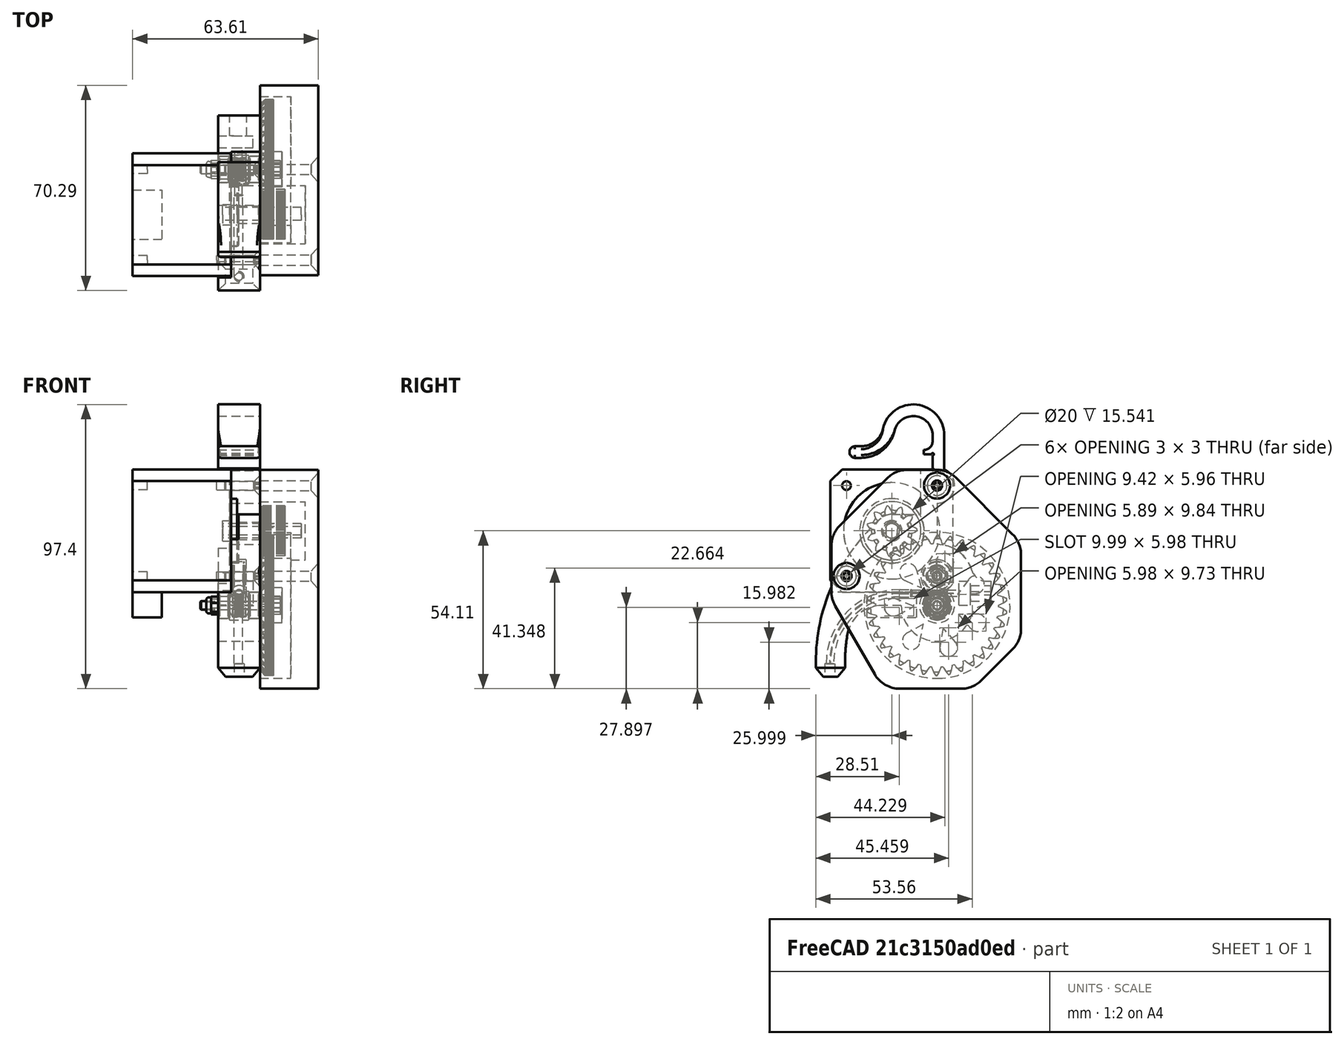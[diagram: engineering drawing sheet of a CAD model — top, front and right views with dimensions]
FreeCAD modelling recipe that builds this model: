
FCSTD DOCUMENT  (FreeCAD 0.14R3692 (Git))
Label: extruder-drive-cover
License: CC-BY 3.0
LicenseURL: http://creativecommons.org/licenses/by/3.0/
objects: Part::Feature×14, Part::Cut×8, Part::Box×5, Part::Cylinder×4, Part::Cone×2, Part::Fuse×2, Part::Fillet×1
note: 36 computed .brp shape members not serialized (recipe doc carries the construction recipe); baked Part::Feature solids carry a one-line shape summary decoded from their .brp

FEATURE [Part::Feature] Part__Feature  label="body"
  Placement = pos=(186.541,257.709,217.11) rot=(0,-1,0;1.5708rad)
  shape: bbox 14.41 x 60.01 x 93.3 mm, 151 faces (baked)
FEATURE [Part::Feature] Part__Feature001  label="washer"
  Placement = pos=(187.041,273.209,191.56) rot=(0,-1,0;1.5708rad)
  shape: bbox 0.5 x 7 x 7 mm, 6 faces (baked)
FEATURE [Part::Feature] Part__Feature002  label="nyloc-nut"
  Placement = pos=(172.141,273.209,191.56) rot=(-0.352103,-0.867206,0.352103;1.7128rad)
  shape: bbox 4 x 6.157 x 6.111 mm, 28 faces (baked)
FEATURE [Part::Feature] Part__Feature003  label="big-gear"
  Placement = pos=(187.041,273.209,191.56) rot=(-0.518458,0.680002,-0.518458;1.94724rad)
  shape: bbox 7 x 47.96 x 48 mm, 571 faces (baked)
FEATURE [Part::Feature] Part__Feature004  label="screw-1"
  Placement = pos=(184.766,273.209,232.61) rot=(0.606758,-0.513506,0.606758;4.09038rad)
  shape: bbox 12 x 6.75 x 6.75 mm, 16 faces (baked)
FEATURE [Part::Feature] Part__Feature005  label="motor"
  Placement = pos=(142.891,257.709,217.11) rot=(0.707107,0,0.707107;3.14159rad)
  shape: bbox 57.75 x 42 x 50.7 mm, 52 faces (baked)
FEATURE [Part::Feature] Part__Feature006  label="hobbed-drive"
  Placement = pos=(176.141,273.209,191.56) rot=(-0.191664,0.962564,-0.191664;1.60894rad)
  shape: bbox 6.4 x 8.762 x 8.754 mm, 204 faces (baked)
FEATURE [Part::Feature] Part__Feature007  label="bearing-1"
  Placement = pos=(178.641,273.209,200.11) rot=(0,-1,0;1.5708rad)
  shape: bbox 4 x 10 x 10 mm, 22 faces (baked)
FEATURE [Part::Feature] Part__Feature008  label="screw-3"
  Placement = pos=(184.766,273.209,201.61) rot=(0.461446,0.757716,0.461446;1.84475rad)
  shape: bbox 12 x 6.75 x 6.75 mm, 16 faces (baked)
FEATURE [Part::Feature] Part__Feature009  label="small-gear"
  Placement = pos=(187.041,257.709,217.11) rot=(-0.050616,0.997435,-0.050616;1.57336rad)
  shape: bbox 8 x 17.12 x 17.19 mm, 199 faces (baked)
FEATURE [Part::Feature] Part__Feature010  label="M3-hex-head-screw"
  Placement = pos=(191.041,273.209,191.56) rot=(0.359725,0.860928,0.359725;1.71999rad)
  shape: bbox 27.5 x 6.124 x 6.144 mm, 19 faces (baked)
FEATURE [Part::Feature] Part__Feature011  label="screw-2"
  Placement = pos=(184.766,242.209,201.61) rot=(0.39302,0.831306,0.39302;1.75451rad)
  shape: bbox 12 x 6.75 x 6.75 mm, 16 faces (baked)
FEATURE [Part::Feature] Part__Feature012  label="bearing-2"
  Placement = pos=(184.041,273.209,191.56) rot=(0.284525,-0.915473,-0.284525;1.659rad)
  shape: bbox 4 x 9 x 9 mm, 22 faces (baked)
FEATURE [Part::Feature] Part__Feature013  label="bearing-3"
  Placement = pos=(173.641,273.209,191.56) rot=(-0.51151,-0.690445,0.51151;1.93302rad)
  shape: bbox 4 x 9 x 9 mm, 22 faces (baked)
FEATURE [Part::Cylinder] Cylinder
  Angle = 360
  Height = 11
  Placement = pos=(186.041,273.209,191.56) rot=(0,1,0;1.5708rad)
  Radius = 25
FEATURE [Part::Cylinder] Cylinder001
  Angle = 360
  Height = 16
  Placement = pos=(186.041,257.709,217.11) rot=(0,1,0;1.5708rad)
  Radius = 10
FEATURE [Part::Cylinder] Cylinder002
  Angle = 360
  Height = 30
  Placement = pos=(184.766,242.209,201.61) rot=(0,1,0;1.5708rad)
  Radius = 1.75
FEATURE [Part::Box] Box  label="Cube"
  Height = 75
  Length = 20
  Width = 65
FEATURE [Part::Box] Box001  label="Cube001"
  Height = 100
  Length = 30
  Placement = pos=(-1,90,-100) rot=(1,0,0;0.785398rad)
  Width = 100
FEATURE [Part::Cut] Cut
  Base = -> Box
  Tool = -> Box001
FEATURE [Part::Box] Box002  label="Cube002"
  Height = 100
  Length = 30
  Placement = pos=(-1,-40,-100) rot=(1,0,0;0.523599rad)
  Width = 100
FEATURE [Part::Cut] Cut001
  Base = -> Cut
  Tool = -> Box002
FEATURE [Part::Box] Box003  label="Cube003"
  Height = 100
  Length = 30
  Placement = pos=(-1,-33,20) rot=(1,0,0;0.785398rad)
  Width = 100
FEATURE [Part::Cut] Cut002
  Base = -> Cut001
  Tool = -> Box003
FEATURE [Part::Box] Box004  label="Cube004"
  Height = 100
  Length = 30
  Placement = pos=(-1,95,20) rot=(1,0,0;0.785398rad)
  Width = 100
FEATURE [Part::Cut] Cut003
  Base = -> Cut002
  Placement = pos=(186.5,237,163) rot=(0,0,1;0rad)
  Tool = -> Box004
FEATURE [Part::Cut] Cut004
  Base = -> Cut003
  Tool = -> Cylinder
FEATURE [Part::Cut] Cut005
  Base = -> Cut004
  Tool = -> Cylinder001
FEATURE [Part::Fillet] Fillet
  Base = -> Cut005
  Edges = 8 edges r=10: [Edge12,Edge14,Edge16,Edge18,Edge20,Edge22,Edge24,Edge26]
FEATURE [Part::Cone] Cone
  Angle = 360
  Height = 3
  Placement = pos=(204,242.209,201.61) rot=(0,1,0;1.5708rad)
  Radius1 = 1.75
  Radius2 = 5
FEATURE [Part::Fuse] Fusion
  Base = -> Cylinder002
  Tool = -> Cone
FEATURE [Part::Cylinder] Cylinder003
  Angle = 360
  Height = 30
  Placement = pos=(184.766,242.209,201.61) rot=(0,1,0;1.5708rad)
  Radius = 1.75
FEATURE [Part::Cone] Cone001
  Angle = 360
  Height = 3
  Placement = pos=(204,242.209,201.61) rot=(0,1,0;1.5708rad)
  Radius1 = 1.75
  Radius2 = 5
FEATURE [Part::Fuse] Fusion001
  Base = -> Cylinder003
  Placement = pos=(0,31,31) rot=(0,0,1;0rad)
  Tool = -> Cone001
FEATURE [Part::Cut] Cut006
  Base = -> Fillet
  Tool = -> Fusion
FEATURE [Part::Cut] Cut007  label="gear-cover"
  Base = -> Cut006
  Tool = -> Fusion001
